# Revit family: Toilet-Elongated-Wall_Hung-American_Standard-Afwall_Millennium-3353.101_3354.101
name_source: partatom
category: Plumbing Fixtures
revit_build: Autodesk Revit 2018 (Build: 20170223_1515(x64)
units: mm (PartAtom-declared; Revit-internal decimal feet)

## family parameters
Cut with Voids When Loaded = No
Host = Face
OmniClass Number = 23.45.05.21.11.11
OmniClass Title = Water Operated Water Closets
Part Type = Normal
Room Calculation Point = No
Round Connector Dimension = Use Radius
Shared = Yes

## types (2) — shared parameters
ADA Compliant = No
Assembly Code = D2010110
Bowl Shape = Elongated
CW Connection = Yes
CWFU = 5
Cold Water Connection Diameter = 1 1/2"
Cold Water Connection Radius = 3/4"
Default Elevation = 15"
Description = Afwall Millenium FloWise Elongated Flushometer Toilet Bowl Only, Back Spud
Finish = Vitreous China-American Standard-020-White
Flush Rate = 1.1gpf to 1.6 gpf (4.2Lpf to 6.0Lpf)
HW Connection = No
Height = 13"
IAPMO Compliance = ASME A112.19.2/CSA B45.1 for Vitreous China Fixtures
Installation Type = Wall Mounted
Length = 26"
Manufacturer = American Standard
Material = Vitreous China-American Standard-020-White
Price = Prices may vary. Please consult Manufacturer Representative for most up-to-date price list.
Product Documentation Link = https://americanstandard.box.com
Product Page URL = https://www.americanstandard-us.com
Recommended Working Pressure = between 25 psi at valve when flushing and 80 psi static
Revised Date = 11/12/2021
Specify ADA Height = 18"
URL = http://www.americanstandard-us.com
Vent Connection = No
WFU = 5
Waste Connection = Yes
Waste Connection Diameter = 2 1/8"
Waste Connection Radius = 1 1/16"
Width = 14"
zero-valued in all types: HWFU

## per-type parameters (varying)
| type | Slotted rim for bedpan holding. |
| 3353.101 | No |
| 3354.101 | Yes |

note: column(s) folded — value = type name in every type: Model

## geometry (parser evidence)
native form markers: Sweep x3
no freeform markers — native parametric forms only
